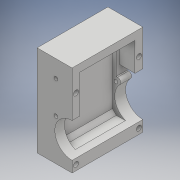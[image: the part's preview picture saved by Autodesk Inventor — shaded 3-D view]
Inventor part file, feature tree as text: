
AUTODESK INVENTOR PART (.ipt)
format: ipt  version: 2018 (Build 220112000, 112)  size: 435,200 bytes
history: native  units: mm
features: sketch x21, projected_geometry x20, extrude x17, hole x4, fillet x3, chamfer x1, mirror x1
ambient origin geometry x8: Origin, YZ Plane, XZ Plane, XY Plane, X Axis, Y Axis, Z Axis, Center Point
bodies: Solid1 (feature_tree)
feature tree (67):
  extrude  "Extrusion1"  Depth=45.0mm
  extrude  "Extrusion2"  Depth=1.95mm
  hole  "Hole1"  [1 undecoded]
  hole  "Hole2"  [1 undecoded]
  fillet  "Fillet1"  Radius=14.0mm
  extrude  "Extrusion3"  Depth=18.5mm
  extrude  "Extrusion4"  Depth=10.0mm
  extrude  "Extrusion5"  Depth=2.0mm
  extrude  "Extrusion6"  Depth=2.0mm
  hole  "Hole3"  [1 undecoded]
  extrude  "Extrusion7"  Depth=0.5mm
  extrude  "Extrusion8"  Depth=5.0mm TaperAngle=0.0deg
  extrude  "Extrusion9"  Depth=10.0mm
  extrude  "Extrusion10"  Depth=10.0mm
  extrude  "Extrusion11"  Depth=14.5mm
  extrude  "Extrusion12"  Depth=14.5mm
  extrude  "Extrusion13"  Depth=5.0mm
  extrude  "Extrusion14"  Depth=5.0mm
  extrude  "Extrusion15"  Depth=5.0mm
  fillet  "Fillet6"  Radius=5.0mm
  extrude  "Extrusion16"  Depth=14.75mm
  extrude  "Extrusion17"  Depth=2.0mm
  chamfer  "Chamfer1"  Distance=1.0mm
  fillet  "Fillet7"  Radius=20.7mm
  hole  "Hole4"  [1 undecoded]
  mirror  "Mirror1"
  sketch  "Sketch1"  dims[d0=24.5mm d1=45.0mm]
  sketch  "Sketch2"  dims[d2=1.95mm d3=0.0mm d4=2.25mm]
  projected_geometry  "Projected Loop1"
  sketch  "Sketch3"  dims[d5=20.0mm d6=2.25mm]
  projected_geometry  "Projected Loop2"
  sketch  "Sketch4"  dims[d7=5.25mm d8=5.25mm d9=14.0mm]
  projected_geometry  "Projected Loop3"
  sketch  "Sketch5"  dims[d10=5.25mm d11=18.5mm]
  projected_geometry  "Projected Loop4"
  sketch  "Sketch6"  dims[d12=10.0mm d13=0.0mm d14=20.5mm]
  projected_geometry  "Projected Loop5"
  sketch  "Sketch7"  dims[d15=2.0mm d16=2.195mm]
  projected_geometry  "Projected Loop6"
  sketch  "Sketch8"  dims[d17=2.0mm]
  projected_geometry  "Projected Loop7"
  sketch  "Sketch9"  dims[d18=2.4mm d19=6.0mm d20=4.4mm d21=2.0mm d22=90.0deg d23=8.0mm d24=20.594885mm d25=20.5mm]
  projected_geometry  "Projected Loop8"
  projected_geometry  "Projected Loop9"
  sketch  "Sketch10"  dims[d26=26.65mm d27=2.0mm]
  projected_geometry  "Projected Loop10"
  projected_geometry  "Projected Loop11"
  sketch  "Sketch11"  dims[d28=2.0mm]
  projected_geometry  "Projected Loop12"
  sketch  "Sketch12"  dims[d29=2.4mm d30=6.0mm d31=4.4mm d32=2.0mm d33=90.0deg d34=8.0mm d35=20.594885mm d36=0.5mm]
  sketch  "Sketch13"  dims[d37=18.0mm d38=5.0mm d39=0.0mm]
  sketch  "Sketch14"  dims[d41=10.0mm d42=0.0mm d43=24.5mm]
  projected_geometry  "Projected Loop13"
  sketch  "Sketch15"  dims[d44=1.15mm d45=0.0mm d46=10.0mm]
  sketch  "Sketch16"  dims[d47=22.0mm d48=14.5mm]
  projected_geometry  "Projected Loop14"
  sketch  "Sketch17"  dims[d49=20.0mm d50=14.5mm]
  projected_geometry  "Projected Loop15"
  sketch  "Sketch18"  dims[d51=24.5mm d52=5.0mm]
  projected_geometry  "Projected Loop16"
  sketch  "Sketch19"  dims[d53=5.0mm d54=2.25mm]
  projected_geometry  "Projected Loop17"
  sketch  "Sketch20"  dims[d55=2.25mm d56=5.0mm d57=5.0mm]
  projected_geometry  "Projected Loop18"
  sketch  "Sketch21"  dims[d58=9.0mm d59=14.75mm d60=4.0mm d61=1.0mm d62=0.0mm d63=20.7mm d64=2.4mm d65=6.0mm d66=4.4mm d67=2.0mm d68=90.0deg d69=8.0mm d70=20.594885mm d72=32.0mm d73=5.0mm d74=0.0mm d75=1.0mm d76=0.0mm d77=12.25mm d78=0.0mm d80=8.0mm d81=4.5mm d82=0.0mm d84=0.2mm d85=0.0mm d86=22.0mm d87=0.5mm d88=0.0mm d91=8.0mm d92=0.0mm d93=5.0mm d94=0.0mm d95=5.0mm d96=0.0mm d97=2.0mm d98=0.2mm d99=0.0mm d100=0.2mm d101=0.0mm d102=2.5mm d103=2.0mm d104=45.0deg d105=1.5mm d106=8.0mm d107=3.2mm d108=5.029mm d109=6.3mm d110=2.0mm d111=90.0deg d112=7.675mm d113=20.594885mm]
  projected_geometry  "Projected Loop19"
  projected_geometry  "Projected Loop20"
note: 4 required parameter values undecoded (feature->parameter linkage not recoverable at this tier; creation-order binding heuristic only, values carry confidence <= 0.55)
